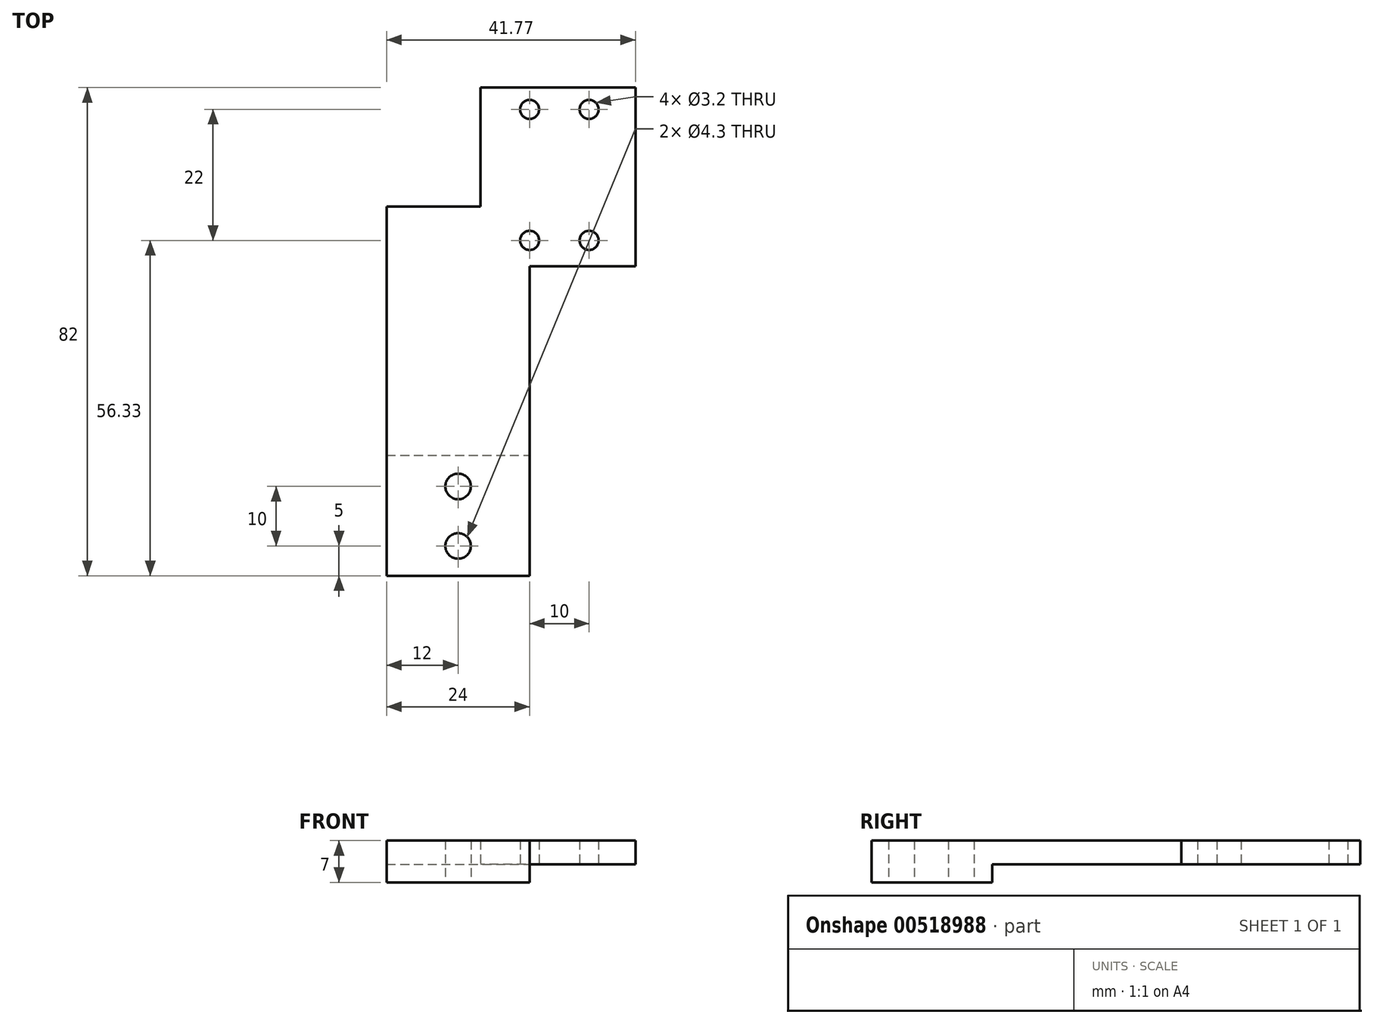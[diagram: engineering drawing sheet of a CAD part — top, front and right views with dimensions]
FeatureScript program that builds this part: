
annotation { "Feature Type Name" : "Feature", "Feature Type Description" : "" }
export const myFeature = defineFeature(function(context is Context, id is Id, definition is map)
    precondition{}
    {
        {
            var Q0;
            Q0=qCreatedBy(makeId("Top.planeOp"),FACE);
            var sketch = newSketch(context, id + "F0", { "sketchPlane" : qUnion([Q0])});
            skLineSegment(sketch, "E0.bottom", {"start": v(-12, -15) * mm, "end": v(12, -15) * mm});
            skLineSegment(sketch, "E0.left", {"start": v(-12, -15) * mm, "end": v(-12, 47) * mm});
            skLineSegment(sketch, "E1", {"start": v(12, 37) * mm, "end": v(29.77, 37) * mm});
            skLineSegment(sketch, "E2", {"start": v(29.77, 37) * mm, "end": v(29.77, 67) * mm});
            skLineSegment(sketch, "E3", {"start": v(29.77, 67) * mm, "end": v(3.77, 67) * mm});
            skCircle(sketch, "E4", {"center": v(0, -10) * mm, "radius": 2.15 * mm});
            skCircle(sketch, "E5", {"center": v(0, 0) * mm, "radius": 2.15 * mm});
            skLineSegment(sketch, "E6", {"start": v(0, -10) * mm, "end": v(12, -10) * mm, "construction": true});
            skLineSegment(sketch, "E7", {"start": v(0, -10) * mm, "end": v(-12, -10) * mm, "construction": true});
            skLineSegment(sketch, "E8", {"start": v(0, -10) * mm, "end": v(0, -15) * mm, "construction": true});
            skCircle(sketch, "E9", {"center": v(12, 63.33) * mm, "radius": 1.6 * mm});
            skCircle(sketch, "E10", {"center": v(12, 41.33) * mm, "radius": 1.6 * mm});
            skCircle(sketch, "E11", {"center": v(22, 41.33) * mm, "radius": 1.6 * mm});
            skCircle(sketch, "E12", {"center": v(22, 63.33) * mm, "radius": 1.6 * mm});
            skLineSegment(sketch, "E13", {"start": v(12, 41.33) * mm, "end": v(12, 63.33) * mm, "construction": true});
            skLineSegment(sketch, "E14", {"start": v(-12, 5.24) * mm, "end": v(12, 5.24) * mm});
            skLineSegment(sketch, "E15", {"start": v(12, -15) * mm, "end": v(12, 37) * mm});
            skLineSegment(sketch, "E16", {"start": v(-12, 47) * mm, "end": v(3.77, 47) * mm});
            skLineSegment(sketch, "E17", {"start": v(3.77, 47) * mm, "end": v(3.77, 67) * mm});
            skSolve(sketch);
        }
        {
            var Q0;
            {var subQ1=sQuery(id+"F0.wireOp",EDGE,"E1");Q0=makeQuery(id+"F0.imprint","IMPRINT",FACE,{"disambiguationData":[TD([[makeQuery(id+"F0.imprint","IMPRINT",EDGE,{"derivedFrom":subQ1}),1.0]])]});}
            var Q1;
            {var subQ1=sQuery(id+"F0.wireOp",EDGE,"E0.bottom");Q1=makeQuery(id+"F0.imprint","IMPRINT",FACE,{"disambiguationData":[TD([[makeQuery(id+"F0.imprint","IMPRINT",EDGE,{"derivedFrom":subQ1}),1.0]])]});}
            var Q2;
            {var subQ4=sQuery(id+"F0.wireOp",EDGE,"E0.top");Q2=makeQuery(id+"F0.imprint","IMPRINT",FACE,{"disambiguationData":[TD([[makeQuery(id+"F0.imprint","IMPRINT",EDGE,{"derivedFrom":subQ4}),-1.0]])]});}
            var Q3;
            Q3=makeQuery(id+"F0.imprint","IMPRINT",FACE,{"disambiguationData":[TD([[makeQuery(id+"F0.imprint","IMPRINT",EDGE,{"derivedFrom":sQuery(id+"F0.wireOp",EDGE,"E5")}),-1.0]])]});
            var Q4;
            Q4=makeQuery(id+"F0.imprint","IMPRINT",FACE,{"disambiguationData":[TD([[makeQuery(id+"F0.imprint","IMPRINT",EDGE,{"derivedFrom":sQuery(id+"F0.wireOp",EDGE,"E4")}),-1.0]])]});
            extrude(context, id + "F1", {"entities" : qUnion([Q0, Q1, Q2, Q3, Q4]), "depth" : 4 * mm, "offsetDistance" : 25 * mm});
        }
        {
            var Q0;
            Q0=makeQuery(id+"F0.imprint","IMPRINT",FACE,{"disambiguationData":[TD([[makeQuery(id+"F0.imprint","IMPRINT",EDGE,{"derivedFrom":sQuery(id+"F0.wireOp",EDGE,"E5")}),-1.0]])]});
            var Q1;
            Q1=makeQuery(id+"F0.imprint","IMPRINT",FACE,{"disambiguationData":[TD([[makeQuery(id+"F0.imprint","IMPRINT",EDGE,{"derivedFrom":sQuery(id+"F0.wireOp",EDGE,"E4")}),-1.0]])]});
            extrude(context, id + "F2", {"entities" : qUnion([Q0, Q1]), "operationType" : NewBodyOperationType.ADD, "oppositeDirection" : true, "depth" : 3 * mm, "offsetDistance" : 25 * mm});
        }
    });
